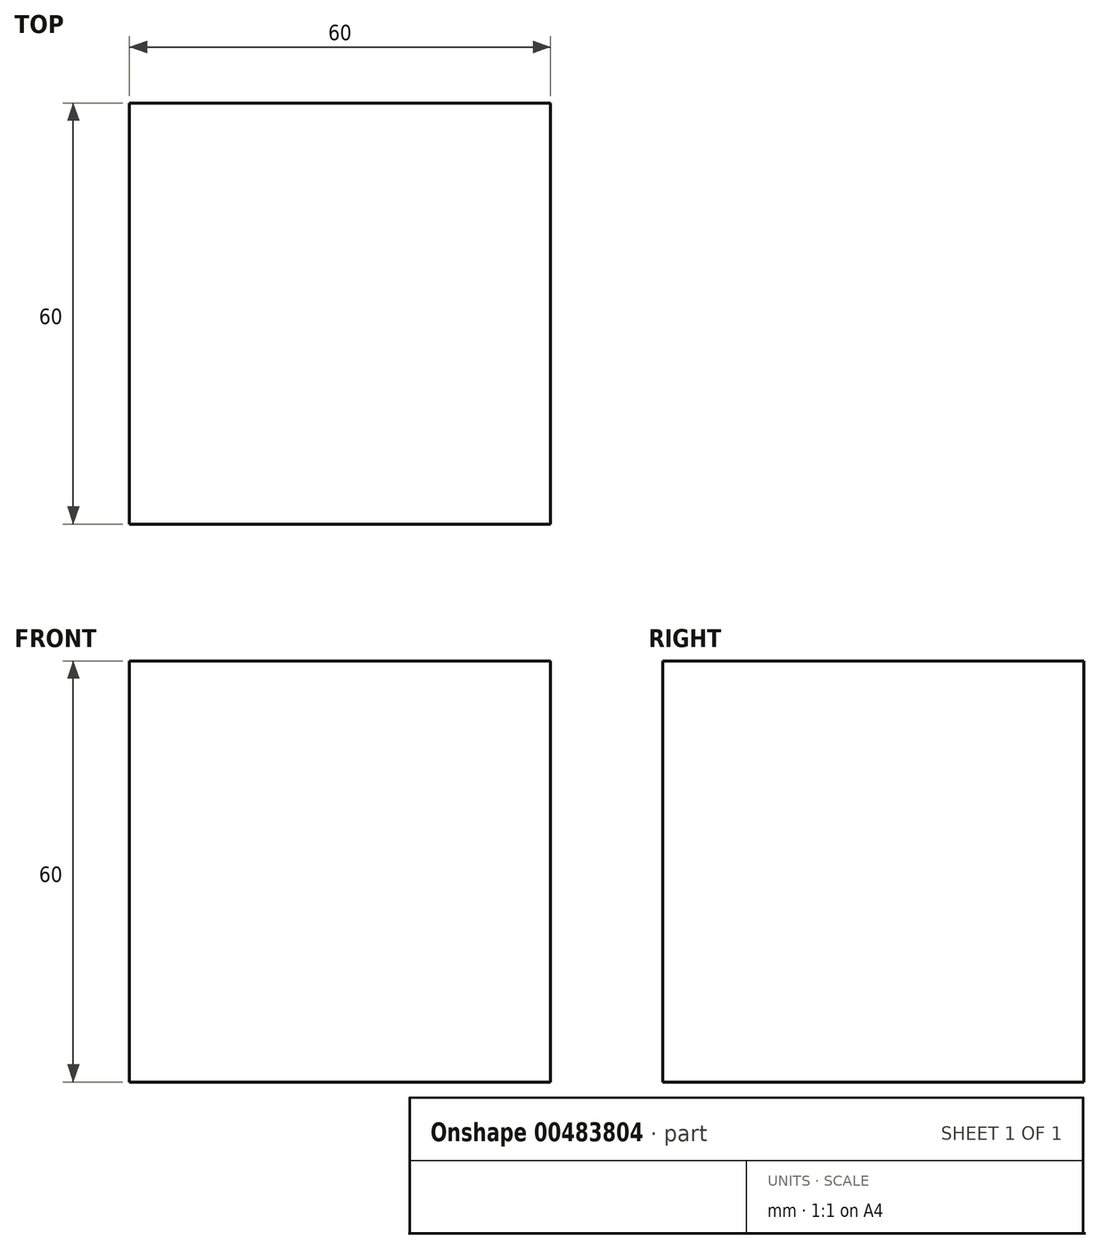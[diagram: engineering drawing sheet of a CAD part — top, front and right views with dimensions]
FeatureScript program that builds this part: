
annotation { "Feature Type Name" : "Feature", "Feature Type Description" : "" }
export const myFeature = defineFeature(function(context is Context, id is Id, definition is map)
    precondition{}
    {
        {
            var Q0;
            Q0=qCreatedBy(makeId("Top.planeOp"),FACE);
            var sketch = newSketch(context, id + "F0", { "sketchPlane" : qUnion([Q0])});
            skLineSegment(sketch, "E0.bottom", {"start": v(30, 30) * mm, "end": v(-30, 30) * mm});
            skLineSegment(sketch, "E0.top", {"start": v(30, -30) * mm, "end": v(-30, -30) * mm});
            skLineSegment(sketch, "E0.left", {"start": v(30, 30) * mm, "end": v(30, -30) * mm});
            skLineSegment(sketch, "E0.right", {"start": v(-30, 30) * mm, "end": v(-30, -30) * mm});
            skPoint(sketch, "E0.middle", {"position": v(0, 0) * mm});
            skSolve(sketch);
        }
        {
            var Q0;
            Q0=qSketchRegion(id+"F0",true);
            extrude(context, id + "F1", {"entities" : qUnion([Q0]), "depth" : 60 * mm});
        }
    });
